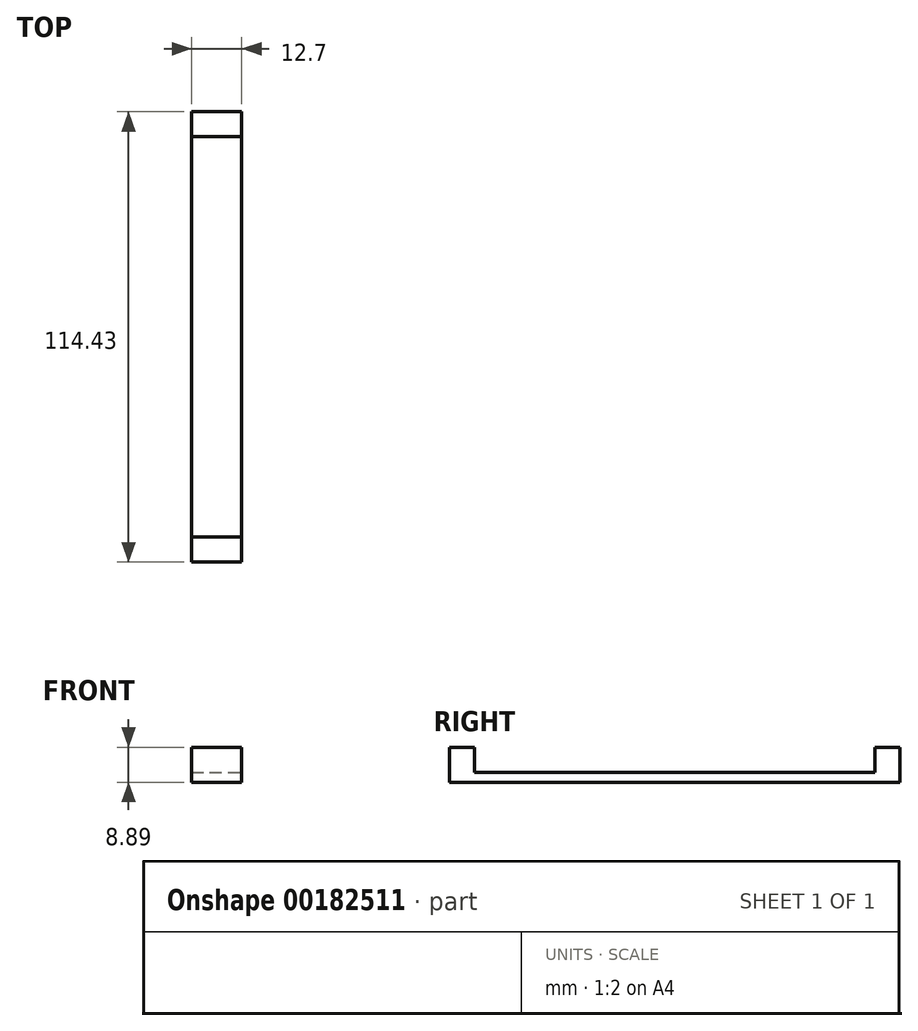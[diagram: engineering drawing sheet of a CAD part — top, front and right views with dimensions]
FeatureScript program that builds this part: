
annotation { "Feature Type Name" : "Feature", "Feature Type Description" : "" }
export const myFeature = defineFeature(function(context is Context, id is Id, definition is map)
    precondition{}
    {
        {
            var Q0;
            Q0=qCreatedBy(makeId("Top.planeOp"),FACE);
            var sketch = newSketch(context, id + "F0", { "sketchPlane" : qUnion([Q0])});
            skLineSegment(sketch, "E0.bottom", {"start": v(-43.9, 50.82) * mm, "end": v(-31.2, 50.82) * mm});
            skLineSegment(sketch, "E0.top", {"start": v(-43.9, -63.6) * mm, "end": v(-31.2, -63.6) * mm});
            skLineSegment(sketch, "E0.left", {"start": v(-43.9, 50.82) * mm, "end": v(-43.9, -63.6) * mm});
            skLineSegment(sketch, "E0.right", {"start": v(-31.2, 50.82) * mm, "end": v(-31.2, -63.6) * mm});
            skSolve(sketch);
        }
        {
            var Q0;
            Q0 = qSketchRegion(id + "F0", true);
            extrude(context, id + "F1", {"entities" : qUnion([Q0]), "depth" : 2.54 * mm});
        }
        {
            var Q0;
            Q0=makeQuery(id+"F1.opExtrude","CAP_FACE",FACE,{"disambiguationData":[OSD([sQuery(id+"F0.wireOp",EDGE,"E0.bottom"),sQuery(id+"F0.wireOp",EDGE,"E0.top"),sQuery(id+"F0.wireOp",EDGE,"E0.left"),sQuery(id+"F0.wireOp",EDGE,"E0.right")])],"isStart":false});
            var sketch = newSketch(context, id + "F2", { "sketchPlane" : qUnion([Q0])});
            skLineSegment(sketch, "E1.bottom", {"start": v(-43.9, 50.82) * mm, "end": v(-31.2, 50.82) * mm});
            skLineSegment(sketch, "E1.top", {"start": v(-43.9, 44.47) * mm, "end": v(-31.2, 44.47) * mm});
            skLineSegment(sketch, "E1.left", {"start": v(-43.9, 50.82) * mm, "end": v(-43.9, 44.47) * mm});
            skLineSegment(sketch, "E1.right", {"start": v(-31.2, 50.82) * mm, "end": v(-31.2, 44.47) * mm});
            skLineSegment(sketch, "E2.bottom", {"start": v(-43.9, -63.6) * mm, "end": v(-31.2, -63.6) * mm});
            skLineSegment(sketch, "E2.top", {"start": v(-43.9, -57.26) * mm, "end": v(-31.2, -57.26) * mm});
            skLineSegment(sketch, "E2.left", {"start": v(-43.9, -63.6) * mm, "end": v(-43.9, -57.26) * mm});
            skLineSegment(sketch, "E2.right", {"start": v(-31.2, -63.6) * mm, "end": v(-31.2, -57.26) * mm});
            skSolve(sketch);
        }
        {
            var Q0;
            Q0 = qSketchRegion(id + "F2", true);
            extrude(context, id + "F3", {"entities" : qUnion([Q0]), "operationType" : NewBodyOperationType.ADD, "depth" : 6.35 * mm});
        }
    });
